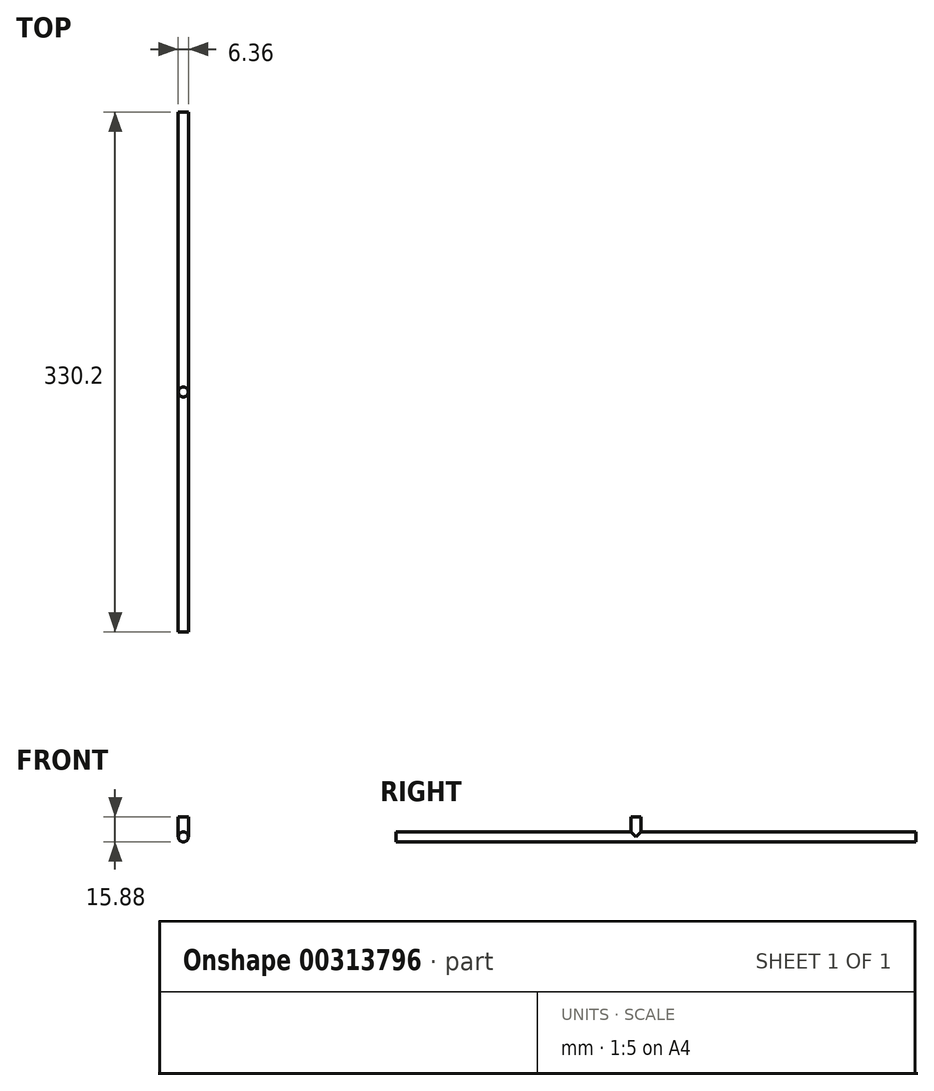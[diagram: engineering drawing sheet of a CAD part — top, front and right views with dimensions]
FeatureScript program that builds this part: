
annotation { "Feature Type Name" : "Feature", "Feature Type Description" : "" }
export const myFeature = defineFeature(function(context is Context, id is Id, definition is map)
    precondition{}
    {
        {
            var Q0;
            Q0=qCreatedBy(makeId("Front.planeOp"),FACE);
            var sketch = newSketch(context, id + "F0", { "sketchPlane" : qUnion([Q0])});
            skCircle(sketch, "E0", {"center": v(0, 0) * mm, "radius": 3.18 * mm});
            skSolve(sketch);
        }
        {
            var Q0;
            Q0 = qSketchRegion(id + "F0", true);
            extrude(context, id + "F1", {"entities" : qUnion([Q0]), "endBound" : BoundingType.SYMMETRIC, "depth" : 330.2 * mm});
        }
        {
            var Q0;
            Q0=qCreatedBy(makeId("Top.planeOp"),FACE);
            var sketch = newSketch(context, id + "F2", { "sketchPlane" : qUnion([Q0])});
            skCircle(sketch, "E1", {"center": v(0, -12.7) * mm, "radius": 3.18 * mm});
            skSolve(sketch);
        }
        {
            var Q0;
            Q0 = qSketchRegion(id + "F2", true);
            extrude(context, id + "F3", {"entities" : qUnion([Q0]), "operationType" : NewBodyOperationType.ADD, "depth" : 12.7 * mm});
        }
    });
